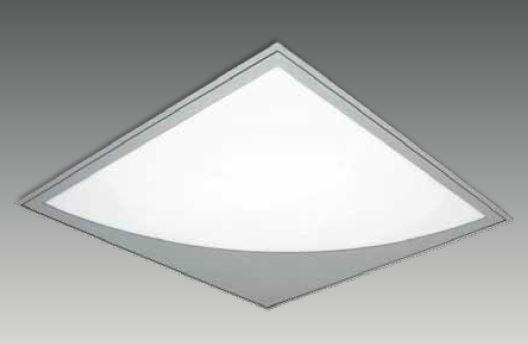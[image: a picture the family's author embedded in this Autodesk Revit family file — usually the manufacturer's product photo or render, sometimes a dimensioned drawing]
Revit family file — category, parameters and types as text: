
# Revit family: G 6060 CIR
name_source: partatom
category: Lighting Fixtures
revit_build: Autodesk Revit 2017 (Build: 20160225_1515(x64)
units: mm (PartAtom-declared; Revit-internal decimal feet)

## family parameters
Always vertical = Yes
Cut with Voids When Loaded = No
Host = Ceiling
Light Source = Yes
OmniClass Number = 23.80.70.11
OmniClass Title = Luminaries for Internal Lighting
Part Type = Normal
Room Calculation Point = No
Round Connector Dimension = Use Diameter
Shared = No

## types (4) — shared parameters
Color Filter = 16777215
Dimming Lamp Color Temperature Shift = <None>
Emit Shape Visible in Rendering = Yes
Emit from Rectangle Length = 570 mm  [stored 1.87008 ft]
Emit from Rectangle Width = 570 mm  [stored 1.87008 ft]
Light Source Symbol Size = 610 mm
Manufacturer = ARLIGHT
Type Image = G 6060 CIR.JPG

## per-type parameters (varying)
| type | Wattage Comments |
| GCIR.6060.36.30 | 36 |
| GCIR.6060.36.40 | 36 |
| GCIR.6060.28.30 | 28 |
| GCIR.6060.28.40 | 28 |

note: [stored X ft] marks values corroborated as IEEE doubles in the binary element streams (Revit-internal decimal feet)

## geometry (parser evidence)
native form markers: Sweep x2
no freeform markers — native parametric forms only
